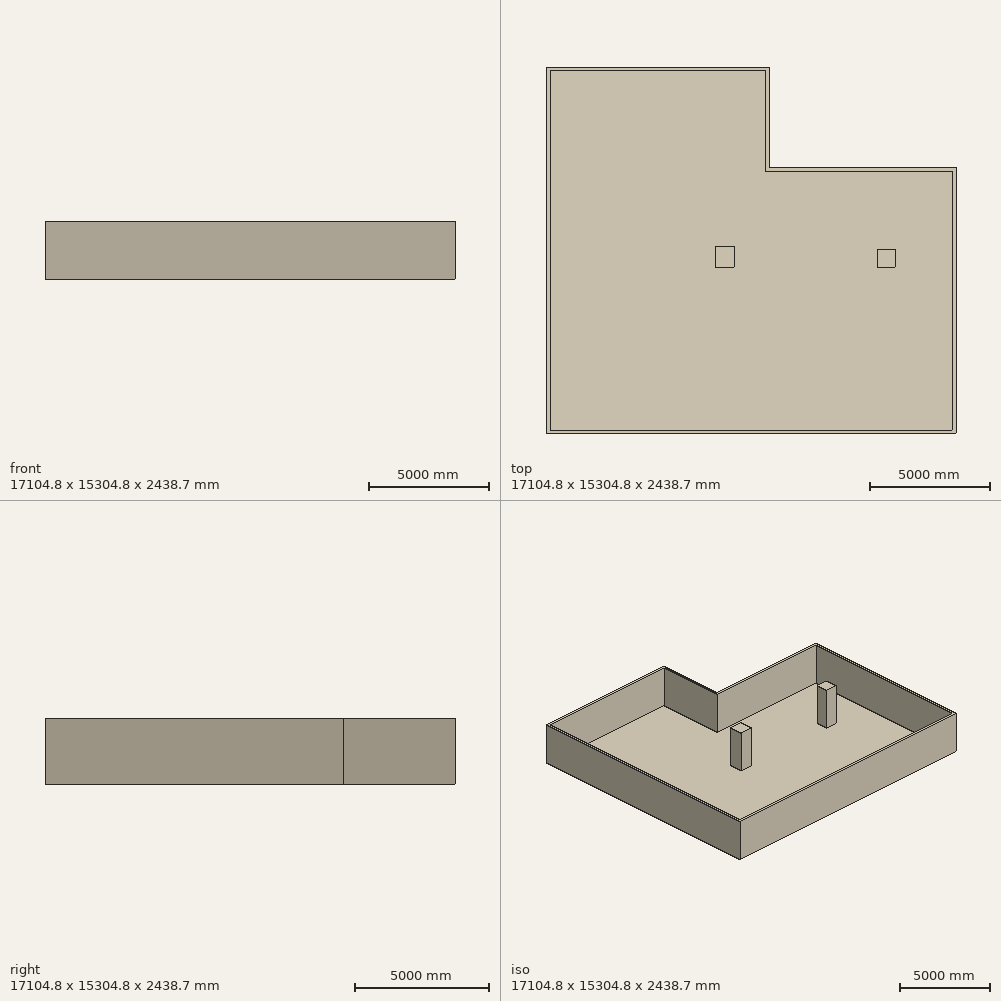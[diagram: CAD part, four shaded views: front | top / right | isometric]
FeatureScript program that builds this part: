
annotation { "Feature Type Name" : "Feature", "Feature Type Description" : "" }
export const myFeature = defineFeature(function(context is Context, id is Id, definition is map)
    precondition{}
    {
        {
            var Q0;
            Q0=qCreatedBy(makeId("Top.planeOp"),FACE);
            var sketch = newSketch(context, id + "F0", { "sketchPlane" : qUnion([Q0])});
            skLineSegment(sketch, "E0", {"start": v(0, 0) * mm, "end": v(16800, 0) * mm});
            skLineSegment(sketch, "E1", {"start": v(16800, 0) * mm, "end": v(16800, 10800) * mm});
            skLineSegment(sketch, "E2", {"start": v(16800, 10800) * mm, "end": v(9000, 10800) * mm});
            skLineSegment(sketch, "E3", {"start": v(9000, 10800) * mm, "end": v(9000, 15000) * mm});
            skLineSegment(sketch, "E4", {"start": v(9000, 15000) * mm, "end": v(0, 15000) * mm});
            skLineSegment(sketch, "E5", {"start": v(0, 15000) * mm, "end": v(0, 0) * mm});
            skLineSegment(sketch, "E6.0", {"start": v(9152.4, 15152.4) * mm, "end": v(-152.4, 15152.4) * mm});
            skLineSegment(sketch, "E6.1", {"start": v(-152.4, -152.4) * mm, "end": v(16952.4, -152.4) * mm});
            skLineSegment(sketch, "E6.2", {"start": v(16952.4, -152.4) * mm, "end": v(16952.4, 10952.4) * mm});
            skLineSegment(sketch, "E6.3", {"start": v(-152.4, 15152.4) * mm, "end": v(-152.4, -152.4) * mm});
            skLineSegment(sketch, "E6.4", {"start": v(16952.4, 10952.4) * mm, "end": v(9152.4, 10952.4) * mm});
            skLineSegment(sketch, "E6.5", {"start": v(9152.4, 10952.4) * mm, "end": v(9152.4, 15152.4) * mm});
            skSolve(sketch);
        }
        {
            var Q0;
            Q0=makeQuery(id+"F0.imprint","IMPRINT",FACE,{"disambiguationData":[TD([[makeQuery(id+"F0.imprint","IMPRINT",EDGE,{"derivedFrom":sQuery(id+"F0.wireOp",EDGE,"E0")}),1.0]])]});
            var sketch = newSketch(context, id + "F1", { "sketchPlane" : qUnion([Q0])});
            skLineSegment(sketch, "E7.bottom", {"start": v(6900, 7650) * mm, "end": v(7700, 7650) * mm});
            skLineSegment(sketch, "E7.top", {"start": v(6900, 6800) * mm, "end": v(7700, 6800) * mm});
            skLineSegment(sketch, "E7.left", {"start": v(6900, 7650) * mm, "end": v(6900, 6800) * mm});
            skLineSegment(sketch, "E7.right", {"start": v(7700, 7650) * mm, "end": v(7700, 6800) * mm});
            skLineSegment(sketch, "E8.bottom", {"start": v(13650, 7550) * mm, "end": v(14400, 7550) * mm});
            skLineSegment(sketch, "E8.top", {"start": v(13650, 6800) * mm, "end": v(14400, 6800) * mm});
            skLineSegment(sketch, "E8.left", {"start": v(13650, 7550) * mm, "end": v(13650, 6800) * mm});
            skLineSegment(sketch, "E8.right", {"start": v(14400, 7550) * mm, "end": v(14400, 6800) * mm});
            skSolve(sketch);
        }
        {
            var Q0;
            Q0=makeQuery(id+"F1.imprint","IMPRINT",FACE,{"disambiguationData":[TD([[makeQuery(id+"F1.imprint","IMPRINT",EDGE,{"derivedFrom":sQuery(id+"F1.wireOp",EDGE,"E7.bottom")}),-1.0]])]});
            var Q1;
            Q1=makeQuery(id+"F0.imprint","IMPRINT",FACE,{"disambiguationData":[TD([[makeQuery(id+"F0.imprint","IMPRINT",EDGE,{"derivedFrom":sQuery(id+"F0.wireOp",EDGE,"E0")}),-1.0]])]});
            var Q2;
            Q2=makeQuery(id+"F1.imprint","IMPRINT",FACE,{"disambiguationData":[TD([[makeQuery(id+"F1.imprint","IMPRINT",EDGE,{"derivedFrom":sQuery(id+"F1.wireOp",EDGE,"E8.bottom")}),-1.0]])]});
            extrude(context, id + "F2", {"entities" : qUnion([Q0, Q1, Q2]), "depth" : 2438.4 * mm});
        }
        {
            var Q0;
            Q0=makeQuery(id+"F2.opExtrude","CAP_FACE",FACE,{"disambiguationData":[OSD([sQuery(id+"F0.wireOp",EDGE,"E0"),sQuery(id+"F0.wireOp",EDGE,"E1"),sQuery(id+"F0.wireOp",EDGE,"E2"),sQuery(id+"F0.wireOp",EDGE,"E3"),sQuery(id+"F0.wireOp",EDGE,"E4"),sQuery(id+"F0.wireOp",EDGE,"E5"),sQuery(id+"F0.wireOp",EDGE,"E6.0"),sQuery(id+"F0.wireOp",EDGE,"E6.1"),sQuery(id+"F0.wireOp",EDGE,"E6.2"),sQuery(id+"F0.wireOp",EDGE,"E6.3"),sQuery(id+"F0.wireOp",EDGE,"E6.4"),sQuery(id+"F0.wireOp",EDGE,"E6.5")])],"isStart":true});
            var sketch = newSketch(context, id + "F3", { "sketchPlane" : qUnion([Q0])});
            skLineSegment(sketch, "E9.0", {"start": v(-152.4, -15152.4) * mm, "end": v(-152.4, 152.4) * mm});
            skLineSegment(sketch, "E9.1", {"start": v(16952.4, 152.4) * mm, "end": v(16952.4, -10952.4) * mm});
            skLineSegment(sketch, "E9.2", {"start": v(16952.4, -10952.4) * mm, "end": v(9152.4, -10952.4) * mm});
            skLineSegment(sketch, "E9.3", {"start": v(-152.4, 152.4) * mm, "end": v(16952.4, 152.4) * mm});
            skLineSegment(sketch, "E9.4", {"start": v(9152.4, -10952.4) * mm, "end": v(9152.4, -15152.4) * mm});
            skLineSegment(sketch, "E9.5", {"start": v(9152.4, -15152.4) * mm, "end": v(-152.4, -15152.4) * mm});
            skSolve(sketch);
        }
        {
            var Q0;
            Q0 = qSketchRegion(id + "F3", true);
            extrude(context, id + "F4", {"entities" : qUnion([Q0]), "depth" : 0.25 * mm});
        }
    });
